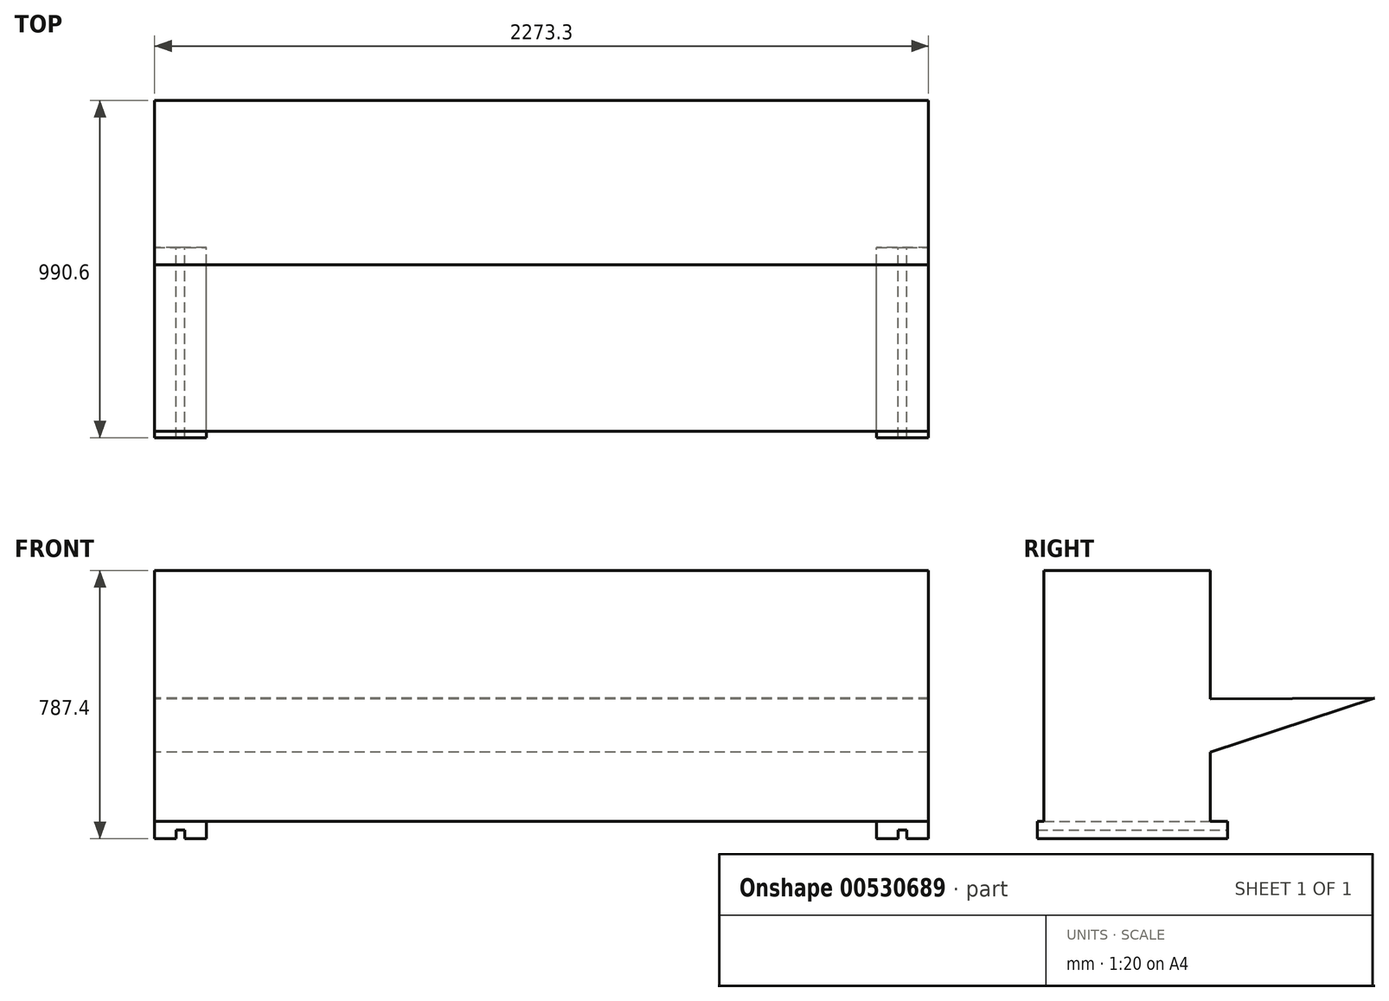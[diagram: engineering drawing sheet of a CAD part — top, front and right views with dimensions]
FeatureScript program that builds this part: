
annotation { "Feature Type Name" : "Feature", "Feature Type Description" : "" }
export const myFeature = defineFeature(function(context is Context, id is Id, definition is map)
    precondition{}
    {
        {
            var Q0;
            Q0=qCreatedBy(makeId("Right.planeOp"),FACE);
            var sketch = newSketch(context, id + "F0", { "sketchPlane" : qUnion([Q0])});
            skLineSegment(sketch, "E0", {"start": v(0, 0) * mm, "end": v(0, 203.2) * mm});
            skLineSegment(sketch, "E1", {"start": v(0, 0) * mm, "end": v(-488.95, 0) * mm});
            skLineSegment(sketch, "E2", {"start": v(-488.95, 0) * mm, "end": v(-488.95, 736.6) * mm});
            skLineSegment(sketch, "E3", {"start": v(482.6, 361.95) * mm, "end": v(0, 203.2) * mm});
            skLineSegment(sketch, "E4", {"start": v(482.6, 361.95) * mm, "end": v(0, 359.8) * mm});
            skLineSegment(sketch, "E5", {"start": v(-488.95, 736.6) * mm, "end": v(0, 736.6) * mm});
            skLineSegment(sketch, "E6", {"start": v(0, 736.6) * mm, "end": v(0, 359.8) * mm});
            skSolve(sketch);
        }
        {
            var Q0;
            Q0=qSketchRegion(id+"F0",true);
            extrude(context, id + "F1", {"entities" : qUnion([Q0]), "depth" : 2273.3 * mm, "offsetDistance" : 25.4 * mm});
        }
        {
            var Q0;
            Q0=qCreatedBy(makeId("Front.planeOp"),FACE);
            var sketch = newSketch(context, id + "F2", { "sketchPlane" : qUnion([Q0])});
            skLineSegment(sketch, "E7", {"start": v(0, 0) * mm, "end": v(76.2, 0) * mm});
            skLineSegment(sketch, "E8", {"start": v(76.2, 0) * mm, "end": v(152.4, 0) * mm});
            skLineSegment(sketch, "E9", {"start": v(152.4, 0) * mm, "end": v(152.4, -50.8) * mm});
            skLineSegment(sketch, "E10", {"start": v(152.4, -50.8) * mm, "end": v(88.9, -50.8) * mm});
            skLineSegment(sketch, "E11", {"start": v(88.9, -50.8) * mm, "end": v(88.9, -25.4) * mm});
            skLineSegment(sketch, "E12", {"start": v(88.9, -25.4) * mm, "end": v(63.5, -25.4) * mm});
            skLineSegment(sketch, "E13", {"start": v(63.5, -25.4) * mm, "end": v(63.5, -50.8) * mm});
            skLineSegment(sketch, "E14", {"start": v(0, -50.8) * mm, "end": v(0, 0) * mm});
            skLineSegment(sketch, "E15", {"start": v(63.5, -50.8) * mm, "end": v(0, -50.8) * mm});
            skLineSegment(sketch, "E16", {"start": v(1136.65, 0) * mm, "end": v(1136.65, 735.11) * mm});
            skLineSegment(sketch, "E17.MirrorCS", {"start": v(2273.3, 0) * mm, "end": v(2197.1, 0) * mm});
            skLineSegment(sketch, "E18.MirrorCS", {"start": v(2197.1, 0) * mm, "end": v(2120.9, 0) * mm});
            skLineSegment(sketch, "E19.MirrorCS", {"start": v(2120.9, 0) * mm, "end": v(2120.9, -50.8) * mm});
            skLineSegment(sketch, "E20.MirrorCS", {"start": v(2120.9, -50.8) * mm, "end": v(2184.4, -50.8) * mm});
            skLineSegment(sketch, "E21.MirrorCS", {"start": v(2184.4, -50.8) * mm, "end": v(2184.4, -25.4) * mm});
            skLineSegment(sketch, "E22.MirrorCS", {"start": v(2184.4, -25.4) * mm, "end": v(2209.8, -25.4) * mm});
            skLineSegment(sketch, "E23.MirrorCS", {"start": v(2209.8, -25.4) * mm, "end": v(2209.8, -50.8) * mm});
            skLineSegment(sketch, "E24.MirrorCS", {"start": v(2209.8, -50.8) * mm, "end": v(2273.3, -50.8) * mm});
            skLineSegment(sketch, "E25.MirrorCS", {"start": v(2273.3, -50.8) * mm, "end": v(2273.3, 0) * mm});
            skSolve(sketch);
        }
        {
            var Q0;
            Q0=qSketchRegion(id+"F2",true);
            extrude(context, id + "F3", {"entities" : qUnion([Q0]), "operationType" : NewBodyOperationType.ADD, "depth" : 508 * mm, "offsetDistance" : 25.4 * mm, "hasSecondDirection" : true, "secondDirectionOppositeDirection" : true, "secondDirectionDepth" : 50.8 * mm});
        }
    });
